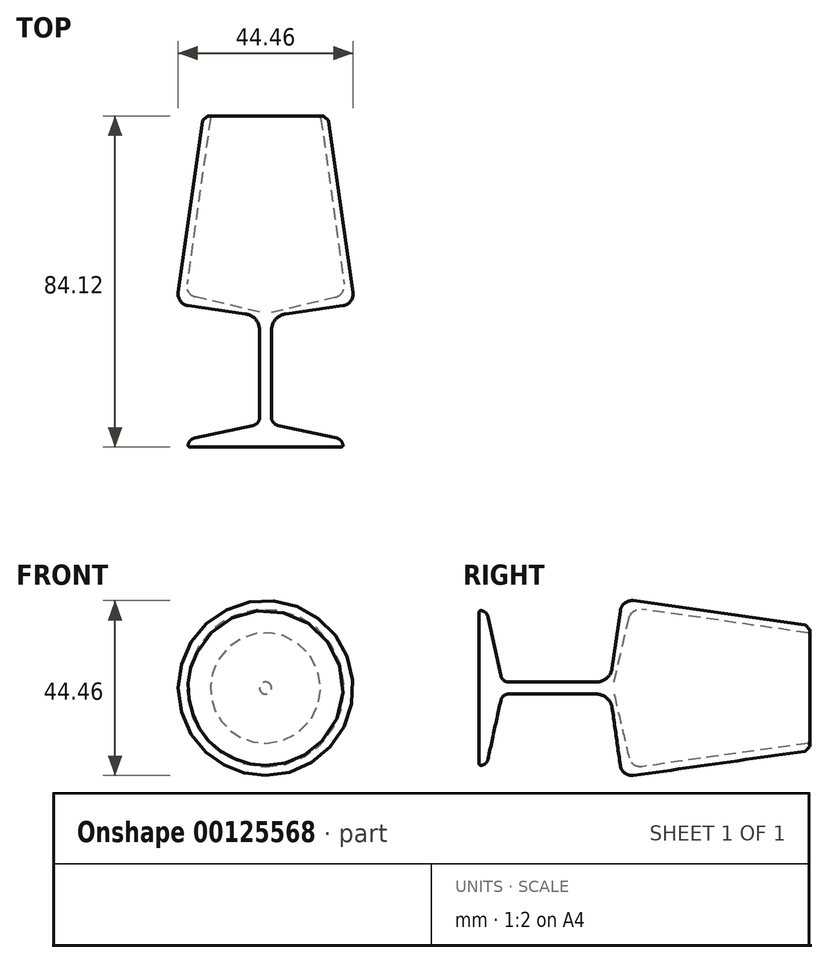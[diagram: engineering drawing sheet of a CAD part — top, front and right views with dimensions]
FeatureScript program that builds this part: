
annotation { "Feature Type Name" : "Feature", "Feature Type Description" : "" }
export const myFeature = defineFeature(function(context is Context, id is Id, definition is map)
    precondition{}
    {
        {
            var Q0;
            Q0=qCreatedBy(makeId("Top.planeOp"),FACE);
            var sketch = newSketch(context, id + "F0", { "sketchPlane" : qUnion([Q0])});
            skLineSegment(sketch, "E0", {"start": v(-16.04, 39.78) * mm, "end": v(-22.2, -3.72) * mm});
            skLineSegment(sketch, "E1", {"start": v(-19.65, -7.12) * mm, "end": v(-5.05, -9.18) * mm});
            skLineSegment(sketch, "E2", {"start": v(-1.53, -13.24) * mm, "end": v(-1.53, -35.52) * mm});
            skLineSegment(sketch, "E3", {"start": v(-3.1, -37.47) * mm, "end": v(-18.1, -40.75) * mm});
            skLineSegment(sketch, "E4", {"start": v(-19.6, -42.21) * mm, "end": v(-19.66, -42.4) * mm});
            skLineSegment(sketch, "E5", {"start": v(-19.17, -43.01) * mm, "end": v(0, -43.01) * mm});
            skLineSegment(sketch, "E6", {"start": v(0, -43.01) * mm, "end": v(0, -10.64) * mm});
            skLineSegment(sketch, "E7", {"start": v(-1.55, -8.7) * mm, "end": v(-17.7, -4.94) * mm});
            skLineSegment(sketch, "E8", {"start": v(-19.98, -1.6) * mm, "end": v(-14.02, 40.54) * mm});
            skLineSegment(sketch, "E9", {"start": v(-14.84, 40.98) * mm, "end": v(-15.87, 40.09) * mm});
            skPoint(sketch, "E10.visualSharp", {"position": v(-22.62, -6.7) * mm});
            skArc(sketch, "E10.filletArc", {"start": v(-22.2, -3.72) * mm, "mid": v(-21.62, -5.95) * mm, "end": v(-19.65, -7.12) * mm});
            skPoint(sketch, "E11.visualSharp", {"position": v(-20.37, -4.32) * mm});
            skArc(sketch, "E11.filletArc", {"start": v(-19.98, -1.6) * mm, "mid": v(-19.49, -3.72) * mm, "end": v(-17.7, -4.94) * mm});
            skPoint(sketch, "E12.visualSharp", {"position": v(-1.53, -37.13) * mm});
            skArc(sketch, "E12.filletArc", {"start": v(-3.1, -37.47) * mm, "mid": v(-1.97, -36.77) * mm, "end": v(-1.53, -35.52) * mm});
            skPoint(sketch, "E13.visualSharp", {"position": v(-19.3, -41.01) * mm});
            skArc(sketch, "E13.filletArc", {"start": v(-18.1, -40.75) * mm, "mid": v(-19.06, -41.26) * mm, "end": v(-19.6, -42.21) * mm});
            skPoint(sketch, "E14.visualSharp", {"position": v(-19.81, -43.01) * mm});
            skArc(sketch, "E14.filletArc", {"start": v(-19.66, -42.4) * mm, "mid": v(-19.57, -42.82) * mm, "end": v(-19.17, -43.01) * mm});
            skPoint(sketch, "E15.visualSharp", {"position": v(-1.53, -9.68) * mm});
            skArc(sketch, "E15.filletArc", {"start": v(-1.53, -13.24) * mm, "mid": v(-2.53, -10.55) * mm, "end": v(-5.05, -9.18) * mm});
            skPoint(sketch, "E16.visualSharp", {"position": v(0, -9.05) * mm});
            skArc(sketch, "E16.filletArc", {"start": v(0, -10.64) * mm, "mid": v(-0.43, -9.4) * mm, "end": v(-1.55, -8.7) * mm});
            skPoint(sketch, "E17.visualSharp", {"position": v(-13.83, 41.87) * mm});
            skArc(sketch, "E17.filletArc", {"start": v(-14.02, 40.54) * mm, "mid": v(-14.28, 41.05) * mm, "end": v(-14.84, 40.98) * mm});
            skPoint(sketch, "E18.visualSharp", {"position": v(-16.01, 39.96) * mm});
            skArc(sketch, "E18.filletArc", {"start": v(-15.87, 40.09) * mm, "mid": v(-15.99, 39.95) * mm, "end": v(-16.04, 39.78) * mm});
            skSolve(sketch);
        }
        {
            var Q0;
            Q0=makeQuery(id+"F0.imprint","IMPRINT",FACE,{"disambiguationData":[TD([[makeQuery(id+"F0.imprint","IMPRINT",EDGE,{"derivedFrom":sQuery(id+"F0.wireOp",EDGE,"E0")}),1.0]])]});
            var Q1;
            Q1=sQuery(id+"F0.wireOp",EDGE,"E6");
            revolve(context, id + "F1", {"entities" : qUnion([Q0]), "axis" : qUnion([Q1]), "revolveType" : RevolveType.FULL});
        }
    });
